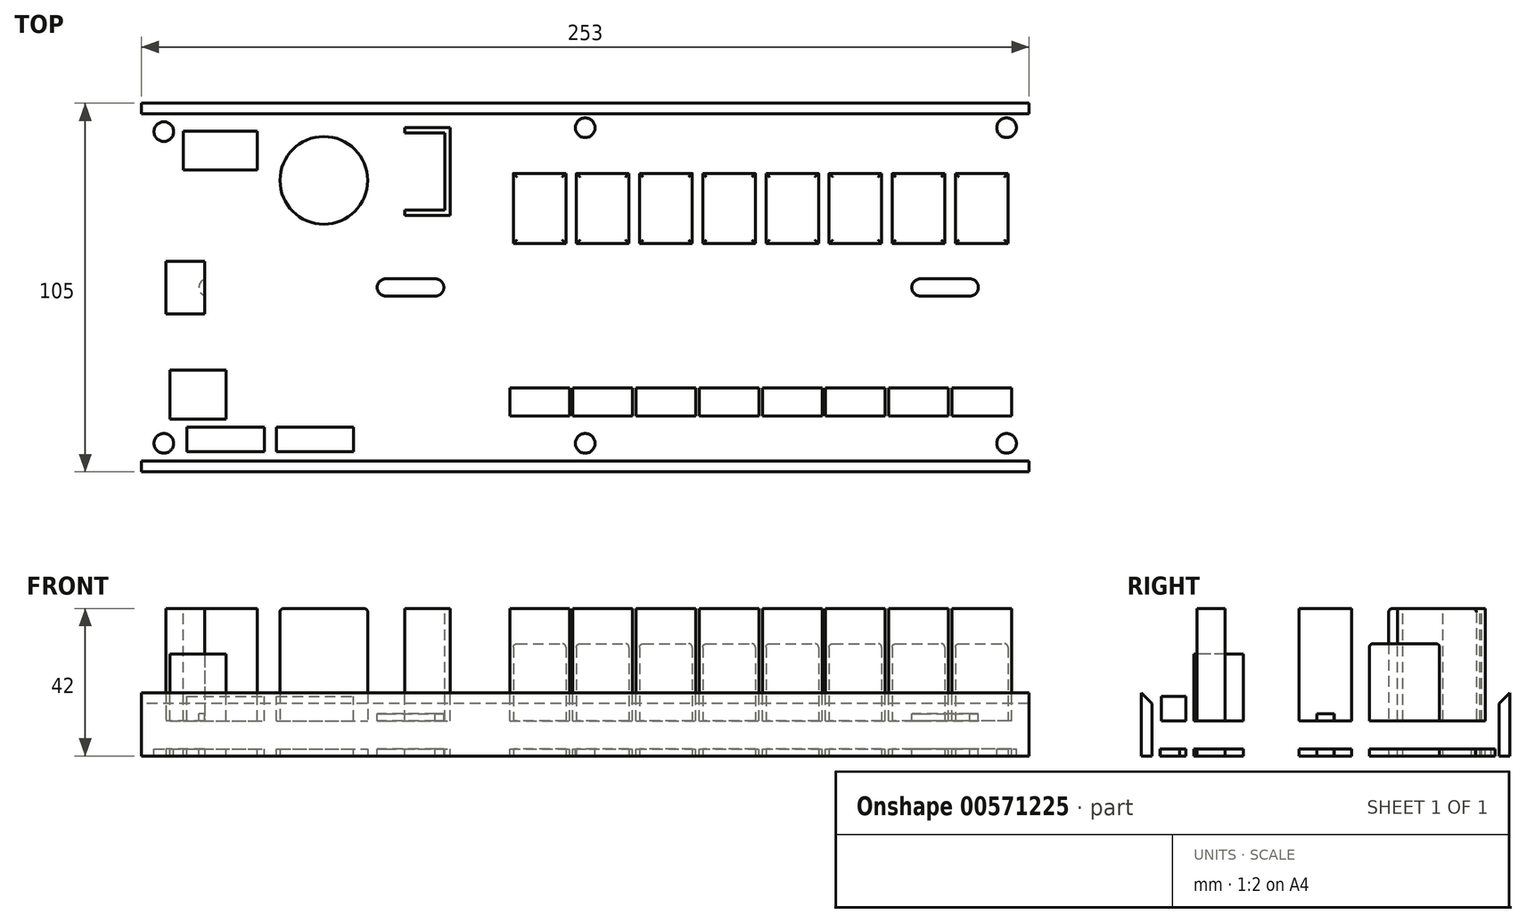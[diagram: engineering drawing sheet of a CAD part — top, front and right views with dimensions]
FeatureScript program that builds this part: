
annotation { "Feature Type Name" : "Feature", "Feature Type Description" : "" }
export const myFeature = defineFeature(function(context is Context, id is Id, definition is map)
    precondition{}
    {
        {
            var Q0;
            Q0=qCreatedBy(makeId("Top.planeOp"),FACE);
            var sketch = newSketch(context, id + "F0", { "sketchPlane" : qUnion([Q0])});
            skLineSegment(sketch, "E0.bottom", {"start": v(126.5, -52.5) * mm, "end": v(-126.5, -52.5) * mm});
            skLineSegment(sketch, "E0.top", {"start": v(126.5, 52.5) * mm, "end": v(-126.5, 52.5) * mm});
            skLineSegment(sketch, "E0.left", {"start": v(126.5, -52.5) * mm, "end": v(126.5, 52.5) * mm});
            skLineSegment(sketch, "E0.right", {"start": v(-126.5, -52.5) * mm, "end": v(-126.5, 52.5) * mm});
            skPoint(sketch, "E0.middle", {"position": v(0, 0) * mm});
            skLineSegment(sketch, "E1.bottom", {"start": v(105.5, 32.5) * mm, "end": v(120.5, 32.5) * mm});
            skLineSegment(sketch, "E1.top", {"start": v(105.5, 12.5) * mm, "end": v(120.5, 12.5) * mm});
            skLineSegment(sketch, "E1.left", {"start": v(105.5, 32.5) * mm, "end": v(105.5, 12.5) * mm});
            skLineSegment(sketch, "E1.right", {"start": v(120.5, 32.5) * mm, "end": v(120.5, 12.5) * mm});
            skPoint(sketch, "E2.oppositeSnap0", {"position": v(113, 12.5) * mm});
            skLineSegment(sketch, "E2.bottom", {"start": v(87.5, 32.5) * mm, "end": v(102.5, 32.5) * mm});
            skLineSegment(sketch, "E2.top", {"start": v(87.5, 12.5) * mm, "end": v(102.5, 12.5) * mm});
            skLineSegment(sketch, "E2.left", {"start": v(87.5, 32.5) * mm, "end": v(87.5, 12.5) * mm});
            skLineSegment(sketch, "E2.right", {"start": v(102.5, 32.5) * mm, "end": v(102.5, 12.5) * mm});
            skLineSegment(sketch, "E3.bottom", {"start": v(69.5, 32.5) * mm, "end": v(84.5, 32.5) * mm});
            skLineSegment(sketch, "E3.top", {"start": v(69.5, 12.5) * mm, "end": v(84.5, 12.5) * mm});
            skLineSegment(sketch, "E3.left", {"start": v(69.5, 32.5) * mm, "end": v(69.5, 12.5) * mm});
            skLineSegment(sketch, "E3.right", {"start": v(84.5, 32.5) * mm, "end": v(84.5, 12.5) * mm});
            skLineSegment(sketch, "E4.bottom", {"start": v(51.5, 32.5) * mm, "end": v(66.5, 32.5) * mm});
            skLineSegment(sketch, "E4.top", {"start": v(51.5, 12.5) * mm, "end": v(66.5, 12.5) * mm});
            skLineSegment(sketch, "E4.left", {"start": v(51.5, 32.5) * mm, "end": v(51.5, 12.5) * mm});
            skLineSegment(sketch, "E4.right", {"start": v(66.5, 32.5) * mm, "end": v(66.5, 12.5) * mm});
            skLineSegment(sketch, "E5.bottom", {"start": v(33.5, 32.5) * mm, "end": v(48.5, 32.5) * mm});
            skLineSegment(sketch, "E5.top", {"start": v(33.5, 12.5) * mm, "end": v(48.5, 12.5) * mm});
            skLineSegment(sketch, "E5.left", {"start": v(33.5, 32.5) * mm, "end": v(33.5, 12.5) * mm});
            skLineSegment(sketch, "E5.right", {"start": v(48.5, 32.5) * mm, "end": v(48.5, 12.5) * mm});
            skPoint(sketch, "E6.oppositeSnap0", {"position": v(41, 12.5) * mm});
            skLineSegment(sketch, "E6.bottom", {"start": v(15.5, 32.5) * mm, "end": v(30.5, 32.5) * mm});
            skLineSegment(sketch, "E6.top", {"start": v(15.5, 12.5) * mm, "end": v(30.5, 12.5) * mm});
            skLineSegment(sketch, "E6.left", {"start": v(15.5, 32.5) * mm, "end": v(15.5, 12.5) * mm});
            skLineSegment(sketch, "E6.right", {"start": v(30.5, 32.5) * mm, "end": v(30.5, 12.5) * mm});
            skLineSegment(sketch, "E7.bottom", {"start": v(-2.5, 32.5) * mm, "end": v(12.5, 32.5) * mm});
            skLineSegment(sketch, "E7.top", {"start": v(-2.5, 12.5) * mm, "end": v(12.5, 12.5) * mm});
            skLineSegment(sketch, "E7.left", {"start": v(-2.5, 32.5) * mm, "end": v(-2.5, 12.5) * mm});
            skLineSegment(sketch, "E7.right", {"start": v(12.5, 32.5) * mm, "end": v(12.5, 12.5) * mm});
            skLineSegment(sketch, "E8.bottom", {"start": v(-20.5, 32.5) * mm, "end": v(-5.5, 32.5) * mm});
            skLineSegment(sketch, "E8.top", {"start": v(-20.5, 12.5) * mm, "end": v(-5.5, 12.5) * mm});
            skLineSegment(sketch, "E8.left", {"start": v(-20.5, 32.5) * mm, "end": v(-20.5, 12.5) * mm});
            skLineSegment(sketch, "E8.right", {"start": v(-5.5, 32.5) * mm, "end": v(-5.5, 12.5) * mm});
            skLineSegment(sketch, "E9.bottom", {"start": v(121.5, -28.68) * mm, "end": v(104.5, -28.68) * mm});
            skLineSegment(sketch, "E9.top", {"start": v(121.5, -36.68) * mm, "end": v(104.5, -36.68) * mm});
            skLineSegment(sketch, "E9.left", {"start": v(121.5, -28.68) * mm, "end": v(121.5, -36.68) * mm});
            skLineSegment(sketch, "E9.right", {"start": v(104.5, -28.68) * mm, "end": v(104.5, -36.68) * mm});
            skLineSegment(sketch, "E10.bottom", {"start": v(86.5, -28.68) * mm, "end": v(103.5, -28.68) * mm});
            skLineSegment(sketch, "E10.top", {"start": v(86.5, -36.68) * mm, "end": v(103.5, -36.68) * mm});
            skLineSegment(sketch, "E10.left", {"start": v(86.5, -28.68) * mm, "end": v(86.5, -36.68) * mm});
            skLineSegment(sketch, "E10.right", {"start": v(103.5, -28.68) * mm, "end": v(103.5, -36.68) * mm});
            skLineSegment(sketch, "E11.bottom", {"start": v(68.5, -28.68) * mm, "end": v(85.5, -28.68) * mm});
            skLineSegment(sketch, "E11.top", {"start": v(68.5, -36.68) * mm, "end": v(85.5, -36.68) * mm});
            skLineSegment(sketch, "E11.left", {"start": v(68.5, -28.68) * mm, "end": v(68.5, -36.68) * mm});
            skLineSegment(sketch, "E11.right", {"start": v(85.5, -28.68) * mm, "end": v(85.5, -36.68) * mm});
            skLineSegment(sketch, "E12.bottom", {"start": v(50.5, -28.68) * mm, "end": v(67.5, -28.68) * mm});
            skLineSegment(sketch, "E12.top", {"start": v(50.5, -36.68) * mm, "end": v(67.5, -36.68) * mm});
            skLineSegment(sketch, "E12.left", {"start": v(50.5, -28.68) * mm, "end": v(50.5, -36.68) * mm});
            skLineSegment(sketch, "E12.right", {"start": v(67.5, -28.68) * mm, "end": v(67.5, -36.68) * mm});
            skLineSegment(sketch, "E13.bottom", {"start": v(32.5, -28.68) * mm, "end": v(49.5, -28.68) * mm});
            skLineSegment(sketch, "E13.top", {"start": v(32.5, -36.68) * mm, "end": v(49.5, -36.68) * mm});
            skLineSegment(sketch, "E13.left", {"start": v(32.5, -28.68) * mm, "end": v(32.5, -36.68) * mm});
            skLineSegment(sketch, "E13.right", {"start": v(49.5, -28.68) * mm, "end": v(49.5, -36.68) * mm});
            skLineSegment(sketch, "E14.bottom", {"start": v(14.5, -28.68) * mm, "end": v(31.5, -28.68) * mm});
            skLineSegment(sketch, "E14.top", {"start": v(14.5, -36.68) * mm, "end": v(31.5, -36.68) * mm});
            skLineSegment(sketch, "E14.left", {"start": v(14.5, -28.68) * mm, "end": v(14.5, -36.68) * mm});
            skLineSegment(sketch, "E14.right", {"start": v(31.5, -28.68) * mm, "end": v(31.5, -36.68) * mm});
            skLineSegment(sketch, "E15.bottom", {"start": v(-3.5, -28.68) * mm, "end": v(13.5, -28.68) * mm});
            skLineSegment(sketch, "E15.top", {"start": v(-3.5, -36.68) * mm, "end": v(13.5, -36.68) * mm});
            skLineSegment(sketch, "E15.left", {"start": v(-3.5, -28.68) * mm, "end": v(-3.5, -36.68) * mm});
            skLineSegment(sketch, "E15.right", {"start": v(13.5, -28.68) * mm, "end": v(13.5, -36.68) * mm});
            skLineSegment(sketch, "E16.bottom", {"start": v(-21.5, -28.68) * mm, "end": v(-4.5, -28.68) * mm});
            skLineSegment(sketch, "E16.top", {"start": v(-21.5, -36.68) * mm, "end": v(-4.5, -36.68) * mm});
            skLineSegment(sketch, "E16.left", {"start": v(-21.5, -28.68) * mm, "end": v(-21.5, -36.68) * mm});
            skLineSegment(sketch, "E16.right", {"start": v(-4.5, -28.68) * mm, "end": v(-4.5, -36.68) * mm});
            skSolve(sketch);
        }
        {
            var Q0;
            Q0=makeQuery(id+"F0.imprint","IMPRINT",FACE,{"disambiguationData":[TD([[makeQuery(id+"F0.imprint","IMPRINT",EDGE,{"derivedFrom":sQuery(id+"F0.wireOp",EDGE,"E8.bottom")}),-1.0]])]});
            var Q1;
            Q1=makeQuery(id+"F0.imprint","IMPRINT",FACE,{"disambiguationData":[TD([[makeQuery(id+"F0.imprint","IMPRINT",EDGE,{"derivedFrom":sQuery(id+"F0.wireOp",EDGE,"E7.bottom")}),-1.0]])]});
            var Q2;
            Q2=makeQuery(id+"F0.imprint","IMPRINT",FACE,{"disambiguationData":[TD([[makeQuery(id+"F0.imprint","IMPRINT",EDGE,{"derivedFrom":sQuery(id+"F0.wireOp",EDGE,"E6.bottom")}),-1.0]])]});
            var Q3;
            Q3=makeQuery(id+"F0.imprint","IMPRINT",FACE,{"disambiguationData":[TD([[makeQuery(id+"F0.imprint","IMPRINT",EDGE,{"derivedFrom":sQuery(id+"F0.wireOp",EDGE,"E5.bottom")}),-1.0]])]});
            var Q4;
            Q4=makeQuery(id+"F0.imprint","IMPRINT",FACE,{"disambiguationData":[TD([[makeQuery(id+"F0.imprint","IMPRINT",EDGE,{"derivedFrom":sQuery(id+"F0.wireOp",EDGE,"E4.bottom")}),-1.0]])]});
            var Q5;
            Q5=makeQuery(id+"F0.imprint","IMPRINT",FACE,{"disambiguationData":[TD([[makeQuery(id+"F0.imprint","IMPRINT",EDGE,{"derivedFrom":sQuery(id+"F0.wireOp",EDGE,"E3.bottom")}),-1.0]])]});
            var Q6;
            Q6=makeQuery(id+"F0.imprint","IMPRINT",FACE,{"disambiguationData":[TD([[makeQuery(id+"F0.imprint","IMPRINT",EDGE,{"derivedFrom":sQuery(id+"F0.wireOp",EDGE,"E2.bottom")}),-1.0]])]});
            var Q7;
            Q7=makeQuery(id+"F0.imprint","IMPRINT",FACE,{"disambiguationData":[TD([[makeQuery(id+"F0.imprint","IMPRINT",EDGE,{"derivedFrom":sQuery(id+"F0.wireOp",EDGE,"E1.bottom")}),-1.0]])]});
            extrude(context, id + "F1", {"entities" : qUnion([Q0, Q1, Q2, Q3, Q4, Q5, Q6, Q7]), "depth" : 32 * mm, "offsetDistance" : 25 * mm});
        }
        {
            var Q0;
            Q0 = qSketchRegion(id + "F0", true);
            extrude(context, id + "F2", {"entities" : qUnion([Q0]), "depth" : 12 * mm, "offsetDistance" : 25 * mm});
        }
        {
            var Q0;
            Q0=makeQuery(id+"F0.imprint","IMPRINT",FACE,{"disambiguationData":[TD([[makeQuery(id+"F0.imprint","IMPRINT",EDGE,{"derivedFrom":sQuery(id+"F0.wireOp",EDGE,"E16.bottom")}),-1.0]])]});
            var Q1;
            Q1=makeQuery(id+"F0.imprint","IMPRINT",FACE,{"disambiguationData":[TD([[makeQuery(id+"F0.imprint","IMPRINT",EDGE,{"derivedFrom":sQuery(id+"F0.wireOp",EDGE,"E15.bottom")}),-1.0]])]});
            var Q2;
            Q2=makeQuery(id+"F0.imprint","IMPRINT",FACE,{"disambiguationData":[TD([[makeQuery(id+"F0.imprint","IMPRINT",EDGE,{"derivedFrom":sQuery(id+"F0.wireOp",EDGE,"E14.bottom")}),-1.0]])]});
            var Q3;
            Q3=makeQuery(id+"F0.imprint","IMPRINT",FACE,{"disambiguationData":[TD([[makeQuery(id+"F0.imprint","IMPRINT",EDGE,{"derivedFrom":sQuery(id+"F0.wireOp",EDGE,"E13.bottom")}),-1.0]])]});
            var Q4;
            Q4=makeQuery(id+"F0.imprint","IMPRINT",FACE,{"disambiguationData":[TD([[makeQuery(id+"F0.imprint","IMPRINT",EDGE,{"derivedFrom":sQuery(id+"F0.wireOp",EDGE,"E12.bottom")}),-1.0]])]});
            var Q5;
            Q5=makeQuery(id+"F0.imprint","IMPRINT",FACE,{"disambiguationData":[TD([[makeQuery(id+"F0.imprint","IMPRINT",EDGE,{"derivedFrom":sQuery(id+"F0.wireOp",EDGE,"E11.bottom")}),-1.0]])]});
            var Q6;
            Q6=makeQuery(id+"F0.imprint","IMPRINT",FACE,{"disambiguationData":[TD([[makeQuery(id+"F0.imprint","IMPRINT",EDGE,{"derivedFrom":sQuery(id+"F0.wireOp",EDGE,"E10.bottom")}),-1.0]])]});
            var Q7;
            Q7=makeQuery(id+"F0.imprint","IMPRINT",FACE,{"disambiguationData":[TD([[makeQuery(id+"F0.imprint","IMPRINT",EDGE,{"derivedFrom":sQuery(id+"F0.wireOp",EDGE,"E9.bottom")}),1.0]])]});
            extrude(context, id + "F3", {"entities" : qUnion([Q0, Q1, Q2, Q3, Q4, Q5, Q6, Q7]), "operationType" : NewBodyOperationType.ADD, "depth" : 42 * mm, "offsetDistance" : 25 * mm});
        }
        {
            var Q0;
            Q0=makeQuery(id+"F2.opExtrude","CAP_FACE",FACE,{"disambiguationData":[OSD([sQuery(id+"F0.wireOp",EDGE,"E0.bottom"),sQuery(id+"F0.wireOp",EDGE,"E0.top"),sQuery(id+"F0.wireOp",EDGE,"E0.left"),sQuery(id+"F0.wireOp",EDGE,"E0.right"),sQuery(id+"F0.wireOp",EDGE,"E1.bottom"),sQuery(id+"F0.wireOp",EDGE,"E1.top"),sQuery(id+"F0.wireOp",EDGE,"E1.left"),sQuery(id+"F0.wireOp",EDGE,"E1.right"),sQuery(id+"F0.wireOp",EDGE,"E2.bottom"),sQuery(id+"F0.wireOp",EDGE,"E2.top"),sQuery(id+"F0.wireOp",EDGE,"E2.left"),sQuery(id+"F0.wireOp",EDGE,"E2.right"),sQuery(id+"F0.wireOp",EDGE,"E3.bottom"),sQuery(id+"F0.wireOp",EDGE,"E3.top"),sQuery(id+"F0.wireOp",EDGE,"E3.left"),sQuery(id+"F0.wireOp",EDGE,"E3.right"),sQuery(id+"F0.wireOp",EDGE,"E4.bottom"),sQuery(id+"F0.wireOp",EDGE,"E4.top"),sQuery(id+"F0.wireOp",EDGE,"E4.left"),sQuery(id+"F0.wireOp",EDGE,"E4.right"),sQuery(id+"F0.wireOp",EDGE,"E5.bottom"),sQuery(id+"F0.wireOp",EDGE,"E5.top"),sQuery(id+"F0.wireOp",EDGE,"E5.left"),sQuery(id+"F0.wireOp",EDGE,"E5.right"),sQuery(id+"F0.wireOp",EDGE,"E6.bottom"),sQuery(id+"F0.wireOp",EDGE,"E6.top"),sQuery(id+"F0.wireOp",EDGE,"E6.left"),sQuery(id+"F0.wireOp",EDGE,"E6.right"),sQuery(id+"F0.wireOp",EDGE,"E7.bottom"),sQuery(id+"F0.wireOp",EDGE,"E7.top"),sQuery(id+"F0.wireOp",EDGE,"E7.left"),sQuery(id+"F0.wireOp",EDGE,"E7.right"),sQuery(id+"F0.wireOp",EDGE,"E8.bottom"),sQuery(id+"F0.wireOp",EDGE,"E8.top"),sQuery(id+"F0.wireOp",EDGE,"E8.left"),sQuery(id+"F0.wireOp",EDGE,"E8.right"),sQuery(id+"F0.wireOp",EDGE,"E9.bottom"),sQuery(id+"F0.wireOp",EDGE,"E9.top"),sQuery(id+"F0.wireOp",EDGE,"E9.left"),sQuery(id+"F0.wireOp",EDGE,"E9.right"),sQuery(id+"F0.wireOp",EDGE,"E10.bottom"),sQuery(id+"F0.wireOp",EDGE,"E10.top"),sQuery(id+"F0.wireOp",EDGE,"E10.left"),sQuery(id+"F0.wireOp",EDGE,"E10.right"),sQuery(id+"F0.wireOp",EDGE,"E11.bottom"),sQuery(id+"F0.wireOp",EDGE,"E11.top"),sQuery(id+"F0.wireOp",EDGE,"E11.left"),sQuery(id+"F0.wireOp",EDGE,"E11.right"),sQuery(id+"F0.wireOp",EDGE,"E12.bottom"),sQuery(id+"F0.wireOp",EDGE,"E12.top"),sQuery(id+"F0.wireOp",EDGE,"E12.left"),sQuery(id+"F0.wireOp",EDGE,"E12.right"),sQuery(id+"F0.wireOp",EDGE,"E13.bottom"),sQuery(id+"F0.wireOp",EDGE,"E13.top"),sQuery(id+"F0.wireOp",EDGE,"E13.left"),sQuery(id+"F0.wireOp",EDGE,"E13.right"),sQuery(id+"F0.wireOp",EDGE,"E14.bottom"),sQuery(id+"F0.wireOp",EDGE,"E14.top"),sQuery(id+"F0.wireOp",EDGE,"E14.left"),sQuery(id+"F0.wireOp",EDGE,"E14.right"),sQuery(id+"F0.wireOp",EDGE,"E15.bottom"),sQuery(id+"F0.wireOp",EDGE,"E15.top"),sQuery(id+"F0.wireOp",EDGE,"E15.left"),sQuery(id+"F0.wireOp",EDGE,"E15.right"),sQuery(id+"F0.wireOp",EDGE,"E16.bottom"),sQuery(id+"F0.wireOp",EDGE,"E16.top"),sQuery(id+"F0.wireOp",EDGE,"E16.left"),sQuery(id+"F0.wireOp",EDGE,"E16.right")])],"isStart":false});
            var sketch = newSketch(context, id + "F4", { "sketchPlane" : qUnion([Q0])});
            skLineSegment(sketch, "E17.bottom", {"start": v(-126.5, 52.5) * mm, "end": v(126.5, 52.5) * mm});
            skLineSegment(sketch, "E17.top", {"start": v(-126.5, 49.5) * mm, "end": v(126.5, 49.5) * mm});
            skLineSegment(sketch, "E17.left", {"start": v(-126.5, 52.5) * mm, "end": v(-126.5, 49.5) * mm});
            skLineSegment(sketch, "E17.right", {"start": v(126.5, 52.5) * mm, "end": v(126.5, 49.5) * mm});
            skLineSegment(sketch, "E18.bottom", {"start": v(-126.5, -52.5) * mm, "end": v(126.5, -52.5) * mm});
            skLineSegment(sketch, "E18.top", {"start": v(-126.5, -49.5) * mm, "end": v(126.5, -49.5) * mm});
            skLineSegment(sketch, "E18.left", {"start": v(-126.5, -52.5) * mm, "end": v(-126.5, -49.5) * mm});
            skLineSegment(sketch, "E18.right", {"start": v(126.5, -52.5) * mm, "end": v(126.5, -49.5) * mm});
            skSolve(sketch);
        }
        {
            var Q0;
            Q0 = qSketchRegion(id + "F4", true);
            extrude(context, id + "F5", {"entities" : qUnion([Q0]), "operationType" : NewBodyOperationType.ADD, "depth" : 6 * mm, "offsetDistance" : 25 * mm});
        }
        {
            var Q0;
            Q0=makeQuery(id+"F5.opExtrude","CAP_EDGE",EDGE,{"disambiguationData":[OSD([sQuery(id+"F4.wireOp",EDGE,"E17.top")])],"isStart":false});
            var Q1;
            Q1=makeQuery(id+"F5.opExtrude","CAP_EDGE",EDGE,{"disambiguationData":[OSD([sQuery(id+"F4.wireOp",EDGE,"E18.top")])],"isStart":false});
            chamfer(context, id + "F6", {"entities" : qUnion([Q0, Q1]), "width" : 3 * mm, "tangentPropagation" : true});
        }
        {
            var Q0;
            Q0=makeQuery(id+"F2.opExtrude","CAP_FACE",FACE,{"disambiguationData":[OSD([sQuery(id+"F0.wireOp",EDGE,"E0.bottom"),sQuery(id+"F0.wireOp",EDGE,"E0.top"),sQuery(id+"F0.wireOp",EDGE,"E0.left"),sQuery(id+"F0.wireOp",EDGE,"E0.right"),sQuery(id+"F0.wireOp",EDGE,"E1.bottom"),sQuery(id+"F0.wireOp",EDGE,"E1.top"),sQuery(id+"F0.wireOp",EDGE,"E1.left"),sQuery(id+"F0.wireOp",EDGE,"E1.right"),sQuery(id+"F0.wireOp",EDGE,"E2.bottom"),sQuery(id+"F0.wireOp",EDGE,"E2.top"),sQuery(id+"F0.wireOp",EDGE,"E2.left"),sQuery(id+"F0.wireOp",EDGE,"E2.right"),sQuery(id+"F0.wireOp",EDGE,"E3.bottom"),sQuery(id+"F0.wireOp",EDGE,"E3.top"),sQuery(id+"F0.wireOp",EDGE,"E3.left"),sQuery(id+"F0.wireOp",EDGE,"E3.right"),sQuery(id+"F0.wireOp",EDGE,"E4.bottom"),sQuery(id+"F0.wireOp",EDGE,"E4.top"),sQuery(id+"F0.wireOp",EDGE,"E4.left"),sQuery(id+"F0.wireOp",EDGE,"E4.right"),sQuery(id+"F0.wireOp",EDGE,"E5.bottom"),sQuery(id+"F0.wireOp",EDGE,"E5.top"),sQuery(id+"F0.wireOp",EDGE,"E5.left"),sQuery(id+"F0.wireOp",EDGE,"E5.right"),sQuery(id+"F0.wireOp",EDGE,"E6.bottom"),sQuery(id+"F0.wireOp",EDGE,"E6.top"),sQuery(id+"F0.wireOp",EDGE,"E6.left"),sQuery(id+"F0.wireOp",EDGE,"E6.right"),sQuery(id+"F0.wireOp",EDGE,"E7.bottom"),sQuery(id+"F0.wireOp",EDGE,"E7.top"),sQuery(id+"F0.wireOp",EDGE,"E7.left"),sQuery(id+"F0.wireOp",EDGE,"E7.right"),sQuery(id+"F0.wireOp",EDGE,"E8.bottom"),sQuery(id+"F0.wireOp",EDGE,"E8.top"),sQuery(id+"F0.wireOp",EDGE,"E8.left"),sQuery(id+"F0.wireOp",EDGE,"E8.right"),sQuery(id+"F0.wireOp",EDGE,"E9.bottom"),sQuery(id+"F0.wireOp",EDGE,"E9.top"),sQuery(id+"F0.wireOp",EDGE,"E9.left"),sQuery(id+"F0.wireOp",EDGE,"E9.right"),sQuery(id+"F0.wireOp",EDGE,"E10.bottom"),sQuery(id+"F0.wireOp",EDGE,"E10.top"),sQuery(id+"F0.wireOp",EDGE,"E10.left"),sQuery(id+"F0.wireOp",EDGE,"E10.right"),sQuery(id+"F0.wireOp",EDGE,"E11.bottom"),sQuery(id+"F0.wireOp",EDGE,"E11.top"),sQuery(id+"F0.wireOp",EDGE,"E11.left"),sQuery(id+"F0.wireOp",EDGE,"E11.right"),sQuery(id+"F0.wireOp",EDGE,"E12.bottom"),sQuery(id+"F0.wireOp",EDGE,"E12.top"),sQuery(id+"F0.wireOp",EDGE,"E12.left"),sQuery(id+"F0.wireOp",EDGE,"E12.right"),sQuery(id+"F0.wireOp",EDGE,"E13.bottom"),sQuery(id+"F0.wireOp",EDGE,"E13.top"),sQuery(id+"F0.wireOp",EDGE,"E13.left"),sQuery(id+"F0.wireOp",EDGE,"E13.right"),sQuery(id+"F0.wireOp",EDGE,"E14.bottom"),sQuery(id+"F0.wireOp",EDGE,"E14.top"),sQuery(id+"F0.wireOp",EDGE,"E14.left"),sQuery(id+"F0.wireOp",EDGE,"E14.right"),sQuery(id+"F0.wireOp",EDGE,"E15.bottom"),sQuery(id+"F0.wireOp",EDGE,"E15.top"),sQuery(id+"F0.wireOp",EDGE,"E15.left"),sQuery(id+"F0.wireOp",EDGE,"E15.right"),sQuery(id+"F0.wireOp",EDGE,"E16.bottom"),sQuery(id+"F0.wireOp",EDGE,"E16.top"),sQuery(id+"F0.wireOp",EDGE,"E16.left"),sQuery(id+"F0.wireOp",EDGE,"E16.right")])],"isStart":false});
            var sketch = newSketch(context, id + "F7", { "sketchPlane" : qUnion([Q0])});
            skLineSegment(sketch, "E19.bottom", {"start": v(-114.5, 44.5) * mm, "end": v(-93.5, 44.5) * mm});
            skLineSegment(sketch, "E19.top", {"start": v(-114.5, 33.5) * mm, "end": v(-93.5, 33.5) * mm});
            skLineSegment(sketch, "E19.left", {"start": v(-114.5, 44.5) * mm, "end": v(-114.5, 33.5) * mm});
            skLineSegment(sketch, "E19.right", {"start": v(-93.5, 44.5) * mm, "end": v(-93.5, 33.5) * mm});
            skLineSegment(sketch, "E20.bottom", {"start": v(-119.5, 7.5) * mm, "end": v(-108.5, 7.5) * mm});
            skLineSegment(sketch, "E20.top", {"start": v(-119.5, -7.5) * mm, "end": v(-108.5, -7.5) * mm});
            skLineSegment(sketch, "E20.left", {"start": v(-119.5, 7.5) * mm, "end": v(-119.5, -7.5) * mm});
            skLineSegment(sketch, "E20.right", {"start": v(-108.5, 7.5) * mm, "end": v(-108.5, -7.5) * mm});
            skCircle(sketch, "E21", {"center": v(-74.5, 30.5) * mm, "radius": 12.5 * mm});
            skLineSegment(sketch, "E22.bottom", {"start": v(-51.5, 45.5) * mm, "end": v(-38.5, 45.5) * mm});
            skLineSegment(sketch, "E22.top", {"start": v(-51.5, 20.5) * mm, "end": v(-38.5, 20.5) * mm});
            skLineSegment(sketch, "E22.left", {"start": v(-51.5, 45.5) * mm, "end": v(-51.5, 20.5) * mm});
            skLineSegment(sketch, "E22.right", {"start": v(-38.5, 45.5) * mm, "end": v(-38.5, 20.5) * mm});
            skLineSegment(sketch, "E23.bottom", {"start": v(-51.5, 44) * mm, "end": v(-40, 44) * mm});
            skLineSegment(sketch, "E23.top", {"start": v(-51.5, 22) * mm, "end": v(-40, 22) * mm});
            skLineSegment(sketch, "E23.left", {"start": v(-51.5, 44) * mm, "end": v(-51.5, 22) * mm});
            skLineSegment(sketch, "E23.right", {"start": v(-40, 44) * mm, "end": v(-40, 22) * mm});
            skSolve(sketch);
        }
        {
            var Q0;
            Q0=makeQuery(id+"F7.imprint","IMPRINT",FACE,{"disambiguationData":[TD([[makeQuery(id+"F7.imprint","IMPRINT",EDGE,{"derivedFrom":sQuery(id+"F7.wireOp",EDGE,"E20.bottom")}),-1.0]])]});
            var Q1;
            Q1=makeQuery(id+"F7.imprint","IMPRINT",FACE,{"disambiguationData":[TD([[makeQuery(id+"F7.imprint","IMPRINT",EDGE,{"derivedFrom":sQuery(id+"F7.wireOp",EDGE,"E19.bottom")}),-1.0]])]});
            var Q2;
            Q2=makeQuery(id+"F7.imprint","IMPRINT",FACE,{"disambiguationData":[TD([[makeQuery(id+"F7.imprint","IMPRINT",EDGE,{"derivedFrom":sQuery(id+"F7.wireOp",EDGE,"E21")}),1.0]])]});
            var Q3;
            {var subQ4=sQuery(id+"F7.wireOp",EDGE,"E22.bottom");Q3=makeQuery(id+"F7.imprint","IMPRINT",FACE,{"disambiguationData":[TD([[makeQuery(id+"F7.imprint","IMPRINT",EDGE,{"derivedFrom":subQ4}),-1.0]])]});}
            extrude(context, id + "F8", {"entities" : qUnion([Q0, Q1, Q2, Q3]), "operationType" : NewBodyOperationType.ADD, "depth" : 30 * mm, "offsetDistance" : 25 * mm});
        }
        {
            var Q0;
            Q0=makeQuery(id+"F8.opExtrude","CAP_EDGE",EDGE,{"disambiguationData":[OSD([sQuery(id+"F7.wireOp",EDGE,"E21")])],"isStart":false});
            var Q1;
            Q1=makeQuery(id+"F1.opExtrude","CAP_FACE",FACE,{"disambiguationData":[OSD([sQuery(id+"F0.wireOp",EDGE,"E8.bottom"),sQuery(id+"F0.wireOp",EDGE,"E8.top"),sQuery(id+"F0.wireOp",EDGE,"E8.left"),sQuery(id+"F0.wireOp",EDGE,"E8.right")])],"isStart":false});
            var Q2;
            Q2=makeQuery(id+"F1.opExtrude","CAP_FACE",FACE,{"disambiguationData":[OSD([sQuery(id+"F0.wireOp",EDGE,"E7.bottom"),sQuery(id+"F0.wireOp",EDGE,"E7.top"),sQuery(id+"F0.wireOp",EDGE,"E7.left"),sQuery(id+"F0.wireOp",EDGE,"E7.right")])],"isStart":false});
            var Q3;
            Q3=makeQuery(id+"F1.opExtrude","CAP_FACE",FACE,{"disambiguationData":[OSD([sQuery(id+"F0.wireOp",EDGE,"E6.bottom"),sQuery(id+"F0.wireOp",EDGE,"E6.top"),sQuery(id+"F0.wireOp",EDGE,"E6.left"),sQuery(id+"F0.wireOp",EDGE,"E6.right")])],"isStart":false});
            var Q4;
            Q4=makeQuery(id+"F1.opExtrude","CAP_FACE",FACE,{"disambiguationData":[OSD([sQuery(id+"F0.wireOp",EDGE,"E5.bottom"),sQuery(id+"F0.wireOp",EDGE,"E5.top"),sQuery(id+"F0.wireOp",EDGE,"E5.left"),sQuery(id+"F0.wireOp",EDGE,"E5.right")])],"isStart":false});
            var Q5;
            Q5=makeQuery(id+"F1.opExtrude","CAP_FACE",FACE,{"disambiguationData":[OSD([sQuery(id+"F0.wireOp",EDGE,"E4.bottom"),sQuery(id+"F0.wireOp",EDGE,"E4.top"),sQuery(id+"F0.wireOp",EDGE,"E4.left"),sQuery(id+"F0.wireOp",EDGE,"E4.right")])],"isStart":false});
            var Q6;
            Q6=makeQuery(id+"F1.opExtrude","CAP_FACE",FACE,{"disambiguationData":[OSD([sQuery(id+"F0.wireOp",EDGE,"E3.bottom"),sQuery(id+"F0.wireOp",EDGE,"E3.top"),sQuery(id+"F0.wireOp",EDGE,"E3.left"),sQuery(id+"F0.wireOp",EDGE,"E3.right")])],"isStart":false});
            var Q7;
            Q7=makeQuery(id+"F1.opExtrude","CAP_FACE",FACE,{"disambiguationData":[OSD([sQuery(id+"F0.wireOp",EDGE,"E2.bottom"),sQuery(id+"F0.wireOp",EDGE,"E2.top"),sQuery(id+"F0.wireOp",EDGE,"E2.left"),sQuery(id+"F0.wireOp",EDGE,"E2.right")])],"isStart":false});
            var Q8;
            Q8=makeQuery(id+"F1.opExtrude","CAP_FACE",FACE,{"disambiguationData":[OSD([sQuery(id+"F0.wireOp",EDGE,"E1.bottom"),sQuery(id+"F0.wireOp",EDGE,"E1.top"),sQuery(id+"F0.wireOp",EDGE,"E1.left"),sQuery(id+"F0.wireOp",EDGE,"E1.right")])],"isStart":false});
            fillet(context, id + "F9", {"entities" : qUnion([Q0, Q1, Q2, Q3, Q4, Q5, Q6, Q7, Q8]), "radius" : 1 * mm, "tangentPropagation" : true, "allowEdgeOverflow" : false});
        }
        {
            var Q0;
            Q0=makeQuery(id+"F2.opExtrude","CAP_FACE",FACE,{"disambiguationData":[OSD([sQuery(id+"F0.wireOp",EDGE,"E0.bottom"),sQuery(id+"F0.wireOp",EDGE,"E0.top"),sQuery(id+"F0.wireOp",EDGE,"E0.left"),sQuery(id+"F0.wireOp",EDGE,"E0.right"),sQuery(id+"F0.wireOp",EDGE,"E1.bottom"),sQuery(id+"F0.wireOp",EDGE,"E1.top"),sQuery(id+"F0.wireOp",EDGE,"E1.left"),sQuery(id+"F0.wireOp",EDGE,"E1.right"),sQuery(id+"F0.wireOp",EDGE,"E2.bottom"),sQuery(id+"F0.wireOp",EDGE,"E2.top"),sQuery(id+"F0.wireOp",EDGE,"E2.left"),sQuery(id+"F0.wireOp",EDGE,"E2.right"),sQuery(id+"F0.wireOp",EDGE,"E3.bottom"),sQuery(id+"F0.wireOp",EDGE,"E3.top"),sQuery(id+"F0.wireOp",EDGE,"E3.left"),sQuery(id+"F0.wireOp",EDGE,"E3.right"),sQuery(id+"F0.wireOp",EDGE,"E4.bottom"),sQuery(id+"F0.wireOp",EDGE,"E4.top"),sQuery(id+"F0.wireOp",EDGE,"E4.left"),sQuery(id+"F0.wireOp",EDGE,"E4.right"),sQuery(id+"F0.wireOp",EDGE,"E5.bottom"),sQuery(id+"F0.wireOp",EDGE,"E5.top"),sQuery(id+"F0.wireOp",EDGE,"E5.left"),sQuery(id+"F0.wireOp",EDGE,"E5.right"),sQuery(id+"F0.wireOp",EDGE,"E6.bottom"),sQuery(id+"F0.wireOp",EDGE,"E6.top"),sQuery(id+"F0.wireOp",EDGE,"E6.left"),sQuery(id+"F0.wireOp",EDGE,"E6.right"),sQuery(id+"F0.wireOp",EDGE,"E7.bottom"),sQuery(id+"F0.wireOp",EDGE,"E7.top"),sQuery(id+"F0.wireOp",EDGE,"E7.left"),sQuery(id+"F0.wireOp",EDGE,"E7.right"),sQuery(id+"F0.wireOp",EDGE,"E8.bottom"),sQuery(id+"F0.wireOp",EDGE,"E8.top"),sQuery(id+"F0.wireOp",EDGE,"E8.left"),sQuery(id+"F0.wireOp",EDGE,"E8.right"),sQuery(id+"F0.wireOp",EDGE,"E9.bottom"),sQuery(id+"F0.wireOp",EDGE,"E9.top"),sQuery(id+"F0.wireOp",EDGE,"E9.left"),sQuery(id+"F0.wireOp",EDGE,"E9.right"),sQuery(id+"F0.wireOp",EDGE,"E10.bottom"),sQuery(id+"F0.wireOp",EDGE,"E10.top"),sQuery(id+"F0.wireOp",EDGE,"E10.left"),sQuery(id+"F0.wireOp",EDGE,"E10.right"),sQuery(id+"F0.wireOp",EDGE,"E11.bottom"),sQuery(id+"F0.wireOp",EDGE,"E11.top"),sQuery(id+"F0.wireOp",EDGE,"E11.left"),sQuery(id+"F0.wireOp",EDGE,"E11.right"),sQuery(id+"F0.wireOp",EDGE,"E12.bottom"),sQuery(id+"F0.wireOp",EDGE,"E12.top"),sQuery(id+"F0.wireOp",EDGE,"E12.left"),sQuery(id+"F0.wireOp",EDGE,"E12.right"),sQuery(id+"F0.wireOp",EDGE,"E13.bottom"),sQuery(id+"F0.wireOp",EDGE,"E13.top"),sQuery(id+"F0.wireOp",EDGE,"E13.left"),sQuery(id+"F0.wireOp",EDGE,"E13.right"),sQuery(id+"F0.wireOp",EDGE,"E14.bottom"),sQuery(id+"F0.wireOp",EDGE,"E14.top"),sQuery(id+"F0.wireOp",EDGE,"E14.left"),sQuery(id+"F0.wireOp",EDGE,"E14.right"),sQuery(id+"F0.wireOp",EDGE,"E15.bottom"),sQuery(id+"F0.wireOp",EDGE,"E15.top"),sQuery(id+"F0.wireOp",EDGE,"E15.left"),sQuery(id+"F0.wireOp",EDGE,"E15.right"),sQuery(id+"F0.wireOp",EDGE,"E16.bottom"),sQuery(id+"F0.wireOp",EDGE,"E16.top"),sQuery(id+"F0.wireOp",EDGE,"E16.left"),sQuery(id+"F0.wireOp",EDGE,"E16.right")])],"isStart":false});
            var sketch = newSketch(context, id + "F10", { "sketchPlane" : qUnion([Q0])});
            skLineSegment(sketch, "E24.bottom", {"start": v(-118.33, -23.49) * mm, "end": v(-102.33, -23.49) * mm});
            skLineSegment(sketch, "E24.top", {"start": v(-118.33, -37.49) * mm, "end": v(-102.33, -37.49) * mm});
            skLineSegment(sketch, "E24.left", {"start": v(-118.33, -23.49) * mm, "end": v(-118.33, -37.49) * mm});
            skLineSegment(sketch, "E24.right", {"start": v(-102.33, -23.49) * mm, "end": v(-102.33, -37.49) * mm});
            skSolve(sketch);
        }
        {
            var Q0;
            Q0 = qSketchRegion(id + "F10", true);
            extrude(context, id + "F11", {"entities" : qUnion([Q0]), "operationType" : NewBodyOperationType.ADD, "depth" : 17 * mm, "offsetDistance" : 25 * mm});
        }
        {
            var Q0;
            Q0=makeQuery(id+"F2.opExtrude","CAP_FACE",FACE,{"disambiguationData":[OSD([sQuery(id+"F0.wireOp",EDGE,"E0.bottom"),sQuery(id+"F0.wireOp",EDGE,"E0.top"),sQuery(id+"F0.wireOp",EDGE,"E0.left"),sQuery(id+"F0.wireOp",EDGE,"E0.right"),sQuery(id+"F0.wireOp",EDGE,"E1.bottom"),sQuery(id+"F0.wireOp",EDGE,"E1.top"),sQuery(id+"F0.wireOp",EDGE,"E1.left"),sQuery(id+"F0.wireOp",EDGE,"E1.right"),sQuery(id+"F0.wireOp",EDGE,"E2.bottom"),sQuery(id+"F0.wireOp",EDGE,"E2.top"),sQuery(id+"F0.wireOp",EDGE,"E2.left"),sQuery(id+"F0.wireOp",EDGE,"E2.right"),sQuery(id+"F0.wireOp",EDGE,"E3.bottom"),sQuery(id+"F0.wireOp",EDGE,"E3.top"),sQuery(id+"F0.wireOp",EDGE,"E3.left"),sQuery(id+"F0.wireOp",EDGE,"E3.right"),sQuery(id+"F0.wireOp",EDGE,"E4.bottom"),sQuery(id+"F0.wireOp",EDGE,"E4.top"),sQuery(id+"F0.wireOp",EDGE,"E4.left"),sQuery(id+"F0.wireOp",EDGE,"E4.right"),sQuery(id+"F0.wireOp",EDGE,"E5.bottom"),sQuery(id+"F0.wireOp",EDGE,"E5.top"),sQuery(id+"F0.wireOp",EDGE,"E5.left"),sQuery(id+"F0.wireOp",EDGE,"E5.right"),sQuery(id+"F0.wireOp",EDGE,"E6.bottom"),sQuery(id+"F0.wireOp",EDGE,"E6.top"),sQuery(id+"F0.wireOp",EDGE,"E6.left"),sQuery(id+"F0.wireOp",EDGE,"E6.right"),sQuery(id+"F0.wireOp",EDGE,"E7.bottom"),sQuery(id+"F0.wireOp",EDGE,"E7.top"),sQuery(id+"F0.wireOp",EDGE,"E7.left"),sQuery(id+"F0.wireOp",EDGE,"E7.right"),sQuery(id+"F0.wireOp",EDGE,"E8.bottom"),sQuery(id+"F0.wireOp",EDGE,"E8.top"),sQuery(id+"F0.wireOp",EDGE,"E8.left"),sQuery(id+"F0.wireOp",EDGE,"E8.right"),sQuery(id+"F0.wireOp",EDGE,"E9.bottom"),sQuery(id+"F0.wireOp",EDGE,"E9.top"),sQuery(id+"F0.wireOp",EDGE,"E9.left"),sQuery(id+"F0.wireOp",EDGE,"E9.right"),sQuery(id+"F0.wireOp",EDGE,"E10.bottom"),sQuery(id+"F0.wireOp",EDGE,"E10.top"),sQuery(id+"F0.wireOp",EDGE,"E10.left"),sQuery(id+"F0.wireOp",EDGE,"E10.right"),sQuery(id+"F0.wireOp",EDGE,"E11.bottom"),sQuery(id+"F0.wireOp",EDGE,"E11.top"),sQuery(id+"F0.wireOp",EDGE,"E11.left"),sQuery(id+"F0.wireOp",EDGE,"E11.right"),sQuery(id+"F0.wireOp",EDGE,"E12.bottom"),sQuery(id+"F0.wireOp",EDGE,"E12.top"),sQuery(id+"F0.wireOp",EDGE,"E12.left"),sQuery(id+"F0.wireOp",EDGE,"E12.right"),sQuery(id+"F0.wireOp",EDGE,"E13.bottom"),sQuery(id+"F0.wireOp",EDGE,"E13.top"),sQuery(id+"F0.wireOp",EDGE,"E13.left"),sQuery(id+"F0.wireOp",EDGE,"E13.right"),sQuery(id+"F0.wireOp",EDGE,"E14.bottom"),sQuery(id+"F0.wireOp",EDGE,"E14.top"),sQuery(id+"F0.wireOp",EDGE,"E14.left"),sQuery(id+"F0.wireOp",EDGE,"E14.right"),sQuery(id+"F0.wireOp",EDGE,"E15.bottom"),sQuery(id+"F0.wireOp",EDGE,"E15.top"),sQuery(id+"F0.wireOp",EDGE,"E15.left"),sQuery(id+"F0.wireOp",EDGE,"E15.right"),sQuery(id+"F0.wireOp",EDGE,"E16.bottom"),sQuery(id+"F0.wireOp",EDGE,"E16.top"),sQuery(id+"F0.wireOp",EDGE,"E16.left"),sQuery(id+"F0.wireOp",EDGE,"E16.right")])],"isStart":false});
            var sketch = newSketch(context, id + "F12", { "sketchPlane" : qUnion([Q0])});
            skLineSegment(sketch, "E25.bottom", {"start": v(-113.5, -39.8) * mm, "end": v(-91.5, -39.8) * mm});
            skLineSegment(sketch, "E25.top", {"start": v(-113.5, -46.8) * mm, "end": v(-91.5, -46.8) * mm});
            skLineSegment(sketch, "E25.left", {"start": v(-113.5, -39.8) * mm, "end": v(-113.5, -46.8) * mm});
            skLineSegment(sketch, "E25.right", {"start": v(-91.5, -39.8) * mm, "end": v(-91.5, -46.8) * mm});
            skLineSegment(sketch, "E26.bottom", {"start": v(-88, -39.8) * mm, "end": v(-66, -39.8) * mm});
            skLineSegment(sketch, "E26.top", {"start": v(-88, -46.8) * mm, "end": v(-66, -46.8) * mm});
            skLineSegment(sketch, "E26.left", {"start": v(-88, -39.8) * mm, "end": v(-88, -46.8) * mm});
            skLineSegment(sketch, "E26.right", {"start": v(-66, -39.8) * mm, "end": v(-66, -46.8) * mm});
            skSolve(sketch);
        }
        {
            var Q0;
            Q0 = qSketchRegion(id + "F12", true);
            extrude(context, id + "F13", {"entities" : qUnion([Q0]), "operationType" : NewBodyOperationType.ADD, "depth" : 5 * mm, "offsetDistance" : 25 * mm});
        }
        {
            var Q0;
            Q0=makeQuery(id+"F2.opExtrude","CAP_FACE",FACE,{"disambiguationData":[OSD([sQuery(id+"F0.wireOp",EDGE,"E0.bottom"),sQuery(id+"F0.wireOp",EDGE,"E0.top"),sQuery(id+"F0.wireOp",EDGE,"E0.left"),sQuery(id+"F0.wireOp",EDGE,"E0.right"),sQuery(id+"F0.wireOp",EDGE,"E1.bottom"),sQuery(id+"F0.wireOp",EDGE,"E1.top"),sQuery(id+"F0.wireOp",EDGE,"E1.left"),sQuery(id+"F0.wireOp",EDGE,"E1.right"),sQuery(id+"F0.wireOp",EDGE,"E2.bottom"),sQuery(id+"F0.wireOp",EDGE,"E2.top"),sQuery(id+"F0.wireOp",EDGE,"E2.left"),sQuery(id+"F0.wireOp",EDGE,"E2.right"),sQuery(id+"F0.wireOp",EDGE,"E3.bottom"),sQuery(id+"F0.wireOp",EDGE,"E3.top"),sQuery(id+"F0.wireOp",EDGE,"E3.left"),sQuery(id+"F0.wireOp",EDGE,"E3.right"),sQuery(id+"F0.wireOp",EDGE,"E4.bottom"),sQuery(id+"F0.wireOp",EDGE,"E4.top"),sQuery(id+"F0.wireOp",EDGE,"E4.left"),sQuery(id+"F0.wireOp",EDGE,"E4.right"),sQuery(id+"F0.wireOp",EDGE,"E5.bottom"),sQuery(id+"F0.wireOp",EDGE,"E5.top"),sQuery(id+"F0.wireOp",EDGE,"E5.left"),sQuery(id+"F0.wireOp",EDGE,"E5.right"),sQuery(id+"F0.wireOp",EDGE,"E6.bottom"),sQuery(id+"F0.wireOp",EDGE,"E6.top"),sQuery(id+"F0.wireOp",EDGE,"E6.left"),sQuery(id+"F0.wireOp",EDGE,"E6.right"),sQuery(id+"F0.wireOp",EDGE,"E7.bottom"),sQuery(id+"F0.wireOp",EDGE,"E7.top"),sQuery(id+"F0.wireOp",EDGE,"E7.left"),sQuery(id+"F0.wireOp",EDGE,"E7.right"),sQuery(id+"F0.wireOp",EDGE,"E8.bottom"),sQuery(id+"F0.wireOp",EDGE,"E8.top"),sQuery(id+"F0.wireOp",EDGE,"E8.left"),sQuery(id+"F0.wireOp",EDGE,"E8.right"),sQuery(id+"F0.wireOp",EDGE,"E9.bottom"),sQuery(id+"F0.wireOp",EDGE,"E9.top"),sQuery(id+"F0.wireOp",EDGE,"E9.left"),sQuery(id+"F0.wireOp",EDGE,"E9.right"),sQuery(id+"F0.wireOp",EDGE,"E10.bottom"),sQuery(id+"F0.wireOp",EDGE,"E10.top"),sQuery(id+"F0.wireOp",EDGE,"E10.left"),sQuery(id+"F0.wireOp",EDGE,"E10.right"),sQuery(id+"F0.wireOp",EDGE,"E11.bottom"),sQuery(id+"F0.wireOp",EDGE,"E11.top"),sQuery(id+"F0.wireOp",EDGE,"E11.left"),sQuery(id+"F0.wireOp",EDGE,"E11.right"),sQuery(id+"F0.wireOp",EDGE,"E12.bottom"),sQuery(id+"F0.wireOp",EDGE,"E12.top"),sQuery(id+"F0.wireOp",EDGE,"E12.left"),sQuery(id+"F0.wireOp",EDGE,"E12.right"),sQuery(id+"F0.wireOp",EDGE,"E13.bottom"),sQuery(id+"F0.wireOp",EDGE,"E13.top"),sQuery(id+"F0.wireOp",EDGE,"E13.left"),sQuery(id+"F0.wireOp",EDGE,"E13.right"),sQuery(id+"F0.wireOp",EDGE,"E14.bottom"),sQuery(id+"F0.wireOp",EDGE,"E14.top"),sQuery(id+"F0.wireOp",EDGE,"E14.left"),sQuery(id+"F0.wireOp",EDGE,"E14.right"),sQuery(id+"F0.wireOp",EDGE,"E15.bottom"),sQuery(id+"F0.wireOp",EDGE,"E15.top"),sQuery(id+"F0.wireOp",EDGE,"E15.left"),sQuery(id+"F0.wireOp",EDGE,"E15.right"),sQuery(id+"F0.wireOp",EDGE,"E16.bottom"),sQuery(id+"F0.wireOp",EDGE,"E16.top"),sQuery(id+"F0.wireOp",EDGE,"E16.left"),sQuery(id+"F0.wireOp",EDGE,"E16.right")])],"isStart":false});
            var sketch = newSketch(context, id + "F14", { "sketchPlane" : qUnion([Q0])});
            skCircle(sketch, "E27", {"center": v(-120.1, 44.4) * mm, "radius": 2.8 * mm});
            skCircle(sketch, "E28", {"center": v(-120.1, -44.4) * mm, "radius": 2.8 * mm});
            skCircle(sketch, "E29", {"center": v(0, 45.5) * mm, "radius": 2.8 * mm});
            skPoint(sketch, "E29.centerSnap0", {"position": v(0, 49.5) * mm});
            skCircle(sketch, "E30", {"center": v(0, -44.4) * mm, "radius": 2.8 * mm});
            skCircle(sketch, "E31", {"center": v(120.1, 45.5) * mm, "radius": 2.8 * mm});
            skCircle(sketch, "E32", {"center": v(120.1, -44.4) * mm, "radius": 2.8 * mm});
            skLineSegment(sketch, "E33", {"start": v(-107.62, 2.45) * mm, "end": v(-93.55, 2.45) * mm});
            skLineSegment(sketch, "E34", {"start": v(-93.55, -2.45) * mm, "end": v(-107.65, -2.45) * mm});
            skArc(sketch, "E35", {"start": v(-107.62, 2.45) * mm, "mid": v(-110.1, 0.01) * mm, "end": v(-107.65, -2.45) * mm});
            skArc(sketch, "E36", {"start": v(-93.55, -2.45) * mm, "mid": v(-91.1, 0) * mm, "end": v(-93.55, 2.45) * mm});
            skArc(sketch, "E37.MirrorCS", {"start": v(-56.85, -2.45) * mm, "mid": v(-59.3, 0) * mm, "end": v(-56.85, 2.45) * mm});
            skArc(sketch, "E38.MirrorCS", {"start": v(-42.78, 2.45) * mm, "mid": v(-40.3, 0.02) * mm, "end": v(-42.75, -2.45) * mm});
            skLineSegment(sketch, "E39.MirrorCS", {"start": v(-42.78, 2.45) * mm, "end": v(-56.85, 2.45) * mm});
            skLineSegment(sketch, "E40.MirrorCS", {"start": v(-56.85, -2.45) * mm, "end": v(-42.75, -2.45) * mm});
            skPoint(sketch, "E41.startSnap0", {"position": v(-49.8, -2.45) * mm});
            skLineSegment(sketch, "E42.MirrorCS", {"start": v(8.02, 2.45) * mm, "end": v(-6.05, 2.45) * mm});
            skLineSegment(sketch, "E43.MirrorCS", {"start": v(-6.05, -2.45) * mm, "end": v(8.05, -2.45) * mm});
            skArc(sketch, "E44.MirrorCS", {"start": v(8.02, 2.45) * mm, "mid": v(10.5, 0.02) * mm, "end": v(8.05, -2.45) * mm});
            skArc(sketch, "E45.MirrorCS", {"start": v(-6.05, -2.45) * mm, "mid": v(-8.5, 0) * mm, "end": v(-6.05, 2.45) * mm});
            skLineSegment(sketch, "E46.MirrorCS", {"start": v(58.82, -2.45) * mm, "end": v(44.72, -2.45) * mm});
            skLineSegment(sketch, "E47.MirrorCS", {"start": v(44.75, 2.45) * mm, "end": v(58.82, 2.45) * mm});
            skArc(sketch, "E48.MirrorCS", {"start": v(44.75, 2.45) * mm, "mid": v(42.27, 0.02) * mm, "end": v(44.72, -2.45) * mm});
            skArc(sketch, "E49.MirrorCS", {"start": v(58.82, -2.45) * mm, "mid": v(61.27, 0) * mm, "end": v(58.82, 2.45) * mm});
            skArc(sketch, "E50.MirrorCS", {"start": v(95.52, -2.44) * mm, "mid": v(93.07, 0) * mm, "end": v(95.52, 2.46) * mm});
            skArc(sketch, "E51.MirrorCS", {"start": v(109.6, 2.46) * mm, "mid": v(112.07, 0.02) * mm, "end": v(109.62, -2.44) * mm});
            skPoint(sketch, "E52.MirrorP", {"position": v(51.77, -2.45) * mm});
            skLineSegment(sketch, "E53.MirrorCS", {"start": v(95.52, -2.44) * mm, "end": v(109.62, -2.44) * mm});
            skLineSegment(sketch, "E54.MirrorCS", {"start": v(109.6, 2.46) * mm, "end": v(95.52, 2.46) * mm});
            skSolve(sketch);
        }
        {
            var Q0;
            Q0=makeQuery(id+"F14.imprint","IMPRINT",FACE,{"disambiguationData":[TD([[makeQuery(id+"F14.imprint","IMPRINT",EDGE,{"derivedFrom":sQuery(id+"F14.wireOp",EDGE,"E37.MirrorCS")}),-1.0]])]});
            var Q1;
            Q1=makeQuery(id+"F14.imprint","IMPRINT",FACE,{"disambiguationData":[TD([[makeQuery(id+"F14.imprint","IMPRINT",EDGE,{"derivedFrom":sQuery(id+"F14.wireOp",EDGE,"E42.MirrorCS")}),1.0]])]});
            var Q2;
            Q2=makeQuery(id+"F14.imprint","IMPRINT",FACE,{"disambiguationData":[TD([[makeQuery(id+"F14.imprint","IMPRINT",EDGE,{"derivedFrom":sQuery(id+"F14.wireOp",EDGE,"E46.MirrorCS")}),-1.0]])]});
            var Q3;
            Q3=makeQuery(id+"F14.imprint","IMPRINT",FACE,{"disambiguationData":[TD([[makeQuery(id+"F14.imprint","IMPRINT",EDGE,{"derivedFrom":sQuery(id+"F14.wireOp",EDGE,"E50.MirrorCS")}),-1.0]])]});
            var Q4;
            {var subQ4=sQuery(id+"F14.wireOp",EDGE,"E33");Q4=makeQuery(id+"F14.imprint","IMPRINT",FACE,{"disambiguationData":[TD([[makeQuery(id+"F14.imprint","IMPRINT",EDGE,{"derivedFrom":subQ4}),-1.0]])]});}
            var Q5;
            {var subQ0=sQuery(id+"F14.wireOp",EDGE,"E35");var subQ1=makeQuery(id+"F8.opExtrude","CAP_EDGE",EDGE,{"disambiguationData":[OSD([sQuery(id+"F7.wireOp",EDGE,"E20.right")])],"isStart":true});var subQ2=makeQuery(id+"F14.imprint","INTERSECT",VERTEX,{"disambiguationData":[OD(0.0)],"derivedFrom":[subQ1,subQ0]});Q5=makeQuery(id+"F14.imprint","IMPRINT",FACE,{"disambiguationData":[TD([[makeQuery(id+"F14.imprint","IMPRINT",EDGE,{"disambiguationData":[TD([[subQ2,-1.0]])],"derivedFrom":subQ0}),1.0]])]});}
            extrude(context, id + "F15", {"entities" : qUnion([Q0, Q1, Q2, Q3, Q4, Q5]), "operationType" : NewBodyOperationType.REMOVE, "endBound" : BoundingType.THROUGH_ALL, "oppositeDirection" : true, "depth" : 25 * mm, "offsetDistance" : 25 * mm});
        }
        {
            var Q0;
            Q0=makeQuery(id+"F14.imprint","IMPRINT",FACE,{"disambiguationData":[TD([[makeQuery(id+"F14.imprint","IMPRINT",EDGE,{"derivedFrom":sQuery(id+"F14.wireOp",EDGE,"E27")}),1.0]])]});
            var Q1;
            Q1=makeQuery(id+"F14.imprint","IMPRINT",FACE,{"disambiguationData":[TD([[makeQuery(id+"F14.imprint","IMPRINT",EDGE,{"derivedFrom":sQuery(id+"F14.wireOp",EDGE,"E29")}),1.0]])]});
            var Q2;
            Q2=makeQuery(id+"F14.imprint","IMPRINT",FACE,{"disambiguationData":[TD([[makeQuery(id+"F14.imprint","IMPRINT",EDGE,{"derivedFrom":sQuery(id+"F14.wireOp",EDGE,"E31")}),1.0]])]});
            var Q3;
            Q3=makeQuery(id+"F14.imprint","IMPRINT",FACE,{"disambiguationData":[TD([[makeQuery(id+"F14.imprint","IMPRINT",EDGE,{"derivedFrom":sQuery(id+"F14.wireOp",EDGE,"E32")}),1.0]])]});
            var Q4;
            Q4=makeQuery(id+"F14.imprint","IMPRINT",FACE,{"disambiguationData":[TD([[makeQuery(id+"F14.imprint","IMPRINT",EDGE,{"derivedFrom":sQuery(id+"F14.wireOp",EDGE,"E30")}),1.0]])]});
            var Q5;
            Q5=makeQuery(id+"F14.imprint","IMPRINT",FACE,{"disambiguationData":[TD([[makeQuery(id+"F14.imprint","IMPRINT",EDGE,{"derivedFrom":sQuery(id+"F14.wireOp",EDGE,"E28")}),1.0]])]});
            extrude(context, id + "F16", {"entities" : qUnion([Q0, Q1, Q2, Q3, Q4, Q5]), "operationType" : NewBodyOperationType.REMOVE, "oppositeDirection" : true, "depth" : 9 * mm, "offsetDistance" : 25 * mm});
        }
        {
            var Q0;
            Q0=makeQuery(id+"F5.boolean.opBoolean","MERGE",FACE,{"derivedFrom":[makeQuery(id+"F2.opExtrude","SWEPT_FACE",FACE,{"disambiguationData":[OSD([sQuery(id+"F0.wireOp",EDGE,"E0.right")])]}),makeQuery(id+"F5.opExtrude","SWEPT_FACE",FACE,{"disambiguationData":[OSD([sQuery(id+"F4.wireOp",EDGE,"E17.left")])]}),makeQuery(id+"F5.opExtrude","SWEPT_FACE",FACE,{"disambiguationData":[OSD([sQuery(id+"F4.wireOp",EDGE,"E18.left")])]})]});
            var sketch = newSketch(context, id + "F17", { "sketchPlane" : qUnion([Q0])});
            skLineSegment(sketch, "E55.bottom", {"start": v(-49.5, 2) * mm, "end": v(49.5, 2) * mm});
            skLineSegment(sketch, "E55.top", {"start": v(-49.5, 10) * mm, "end": v(49.5, 10) * mm});
            skLineSegment(sketch, "E55.left", {"start": v(-49.5, 2) * mm, "end": v(-49.5, 10) * mm});
            skLineSegment(sketch, "E55.right", {"start": v(49.5, 2) * mm, "end": v(49.5, 10) * mm});
            skSolve(sketch);
        }
        {
            var Q0;
            Q0=makeQuery(id+"F17.imprint","IMPRINT",FACE,{"disambiguationData":[TD([[makeQuery(id+"F17.imprint","IMPRINT",EDGE,{"derivedFrom":sQuery(id+"F17.wireOp",EDGE,"E55.bottom")}),1.0]])]});
            extrude(context, id + "F18", {"entities" : qUnion([Q0]), "operationType" : NewBodyOperationType.REMOVE, "endBound" : BoundingType.THROUGH_ALL, "oppositeDirection" : true, "depth" : 25 * mm, "offsetDistance" : 25 * mm});
        }
    });
